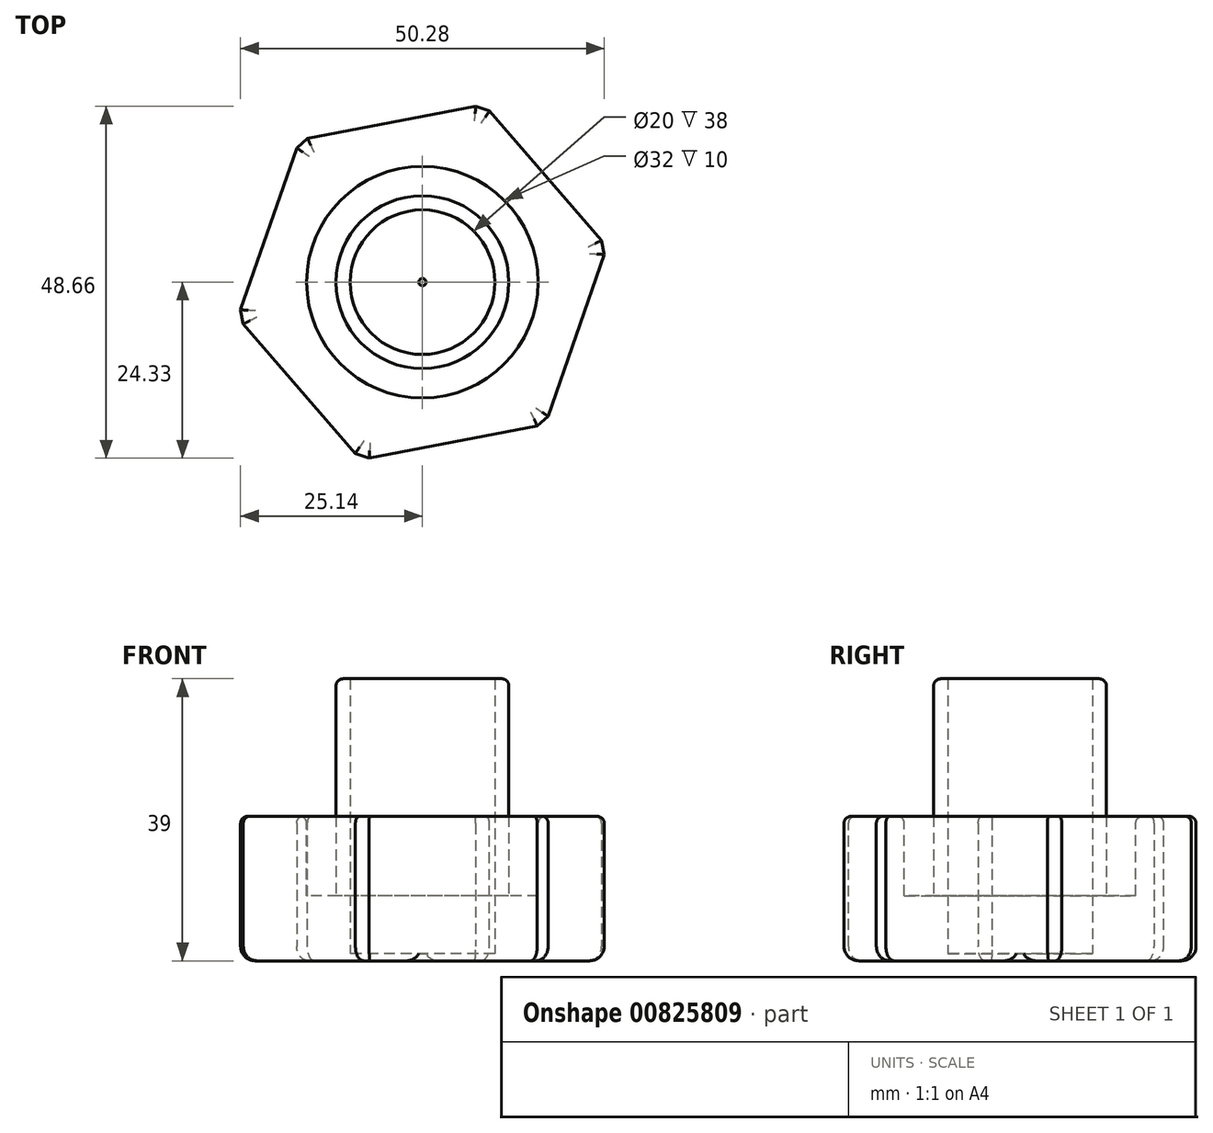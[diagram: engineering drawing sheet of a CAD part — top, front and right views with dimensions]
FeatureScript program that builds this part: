
annotation { "Feature Type Name" : "Feature", "Feature Type Description" : "" }
export const myFeature = defineFeature(function(context is Context, id is Id, definition is map)
    precondition{}
    {
        {
            var Q0;
            Q0=qCreatedBy(makeId("Top.planeOp"),FACE);
            var sketch = newSketch(context, id + "F0", { "sketchPlane" : qUnion([Q0])});
            skCircle(sketch, "E0", {"center": v(0, 0) * mm, "radius": 18.75 * mm});
            skCircle(sketch, "E1", {"center": v(0, 0) * mm, "radius": 10 * mm});
            skSolve(sketch);
        }
        {
            var Q0;
            Q0=makeQuery(id+"F0.imprint","IMPRINT",FACE,{"disambiguationData":[TD([[makeQuery(id+"F0.imprint","IMPRINT",EDGE,{"derivedFrom":sQuery(id+"F0.wireOp",EDGE,"E0")}),1.0]])]});
            extrude(context, id + "F1", {"entities" : qUnion([Q0]), "depth" : 20 * mm, "offsetDistance" : 25 * mm});
        }
        {
            var Q0;
            Q0=makeQuery(id+"F1.opExtrude","CAP_FACE",FACE,{"disambiguationData":[OSD([sQuery(id+"F0.wireOp",EDGE,"E0"),sQuery(id+"F0.wireOp",EDGE,"pwZuV8CJ-bOZG-QT0O-5IBz-90nucOeMPY0X")])],"isStart":false});
            var sketch = newSketch(context, id + "F2", { "sketchPlane" : qUnion([Q0])});
            skCircle(sketch, "E2", {"center": v(0, 0) * mm, "radius": 16 * mm});
            skSolve(sketch);
        }
        {
            var Q0;
            Q0=makeQuery(id+"F2.imprint","IMPRINT",FACE,{"disambiguationData":[TD([[makeQuery(id+"F2.imprint","IMPRINT",EDGE,{"derivedFrom":sQuery(id+"F2.wireOp",EDGE,"E2")}),1.0]])]});
            extrude(context, id + "F3", {"entities" : qUnion([Q0]), "operationType" : NewBodyOperationType.REMOVE, "oppositeDirection" : true, "depth" : 11 * mm, "offsetDistance" : 25 * mm});
        }
        {
            var Q0;
            Q0=makeQuery(id+"F3.boolean.opBoolean","COPY",FACE,{"derivedFrom":makeQuery(id+"F3.opExtrude","CAP_FACE",FACE,{"disambiguationData":[OSD([sQuery(id+"F0.wireOp",EDGE,"E1"),sQuery(id+"F2.wireOp",EDGE,"E2")])],"isStart":false})});
            var sketch = newSketch(context, id + "F4", { "sketchPlane" : qUnion([Q0])});
            skCircle(sketch, "E3", {"center": v(0, 0) * mm, "radius": 11.95 * mm});
            skSolve(sketch);
        }
        {
            var Q0;
            Q0=makeQuery(id+"F4.imprint","IMPRINT",FACE,{"disambiguationData":[TD([[makeQuery(id+"F4.imprint","IMPRINT",EDGE,{"derivedFrom":sQuery(id+"F4.wireOp",EDGE,"E3")}),1.0]])]});
            extrude(context, id + "F5", {"entities" : qUnion([Q0]), "operationType" : NewBodyOperationType.ADD, "depth" : 30 * mm, "offsetDistance" : 25 * mm});
        }
        {
            var Q0;
            Q0=makeQuery(id+"F5.opExtrude","CAP_EDGE",EDGE,{"disambiguationData":[OSD([sQuery(id+"F4.wireOp",EDGE,"E3")])],"isStart":false});
            fillet(context, id + "F6", {"entities" : qUnion([Q0]), "radius" : 1 * mm, "tangentPropagation" : true, "allowEdgeOverflow" : false});
        }
        {
            var Q0;
            Q0=makeQuery(id+"F1.opExtrude","CAP_FACE",FACE,{"disambiguationData":[OSD([sQuery(id+"F0.wireOp",EDGE,"E0"),sQuery(id+"F0.wireOp",EDGE,"pwZuV8CJ-bOZG-QT0O-5IBz-90nucOeMPY0X")])],"isStart":true});
            var sketch = newSketch(context, id + "F7", { "sketchPlane" : qUnion([Q0])});
            skCircle(sketch, "E4", {"center": v(0, 0) * mm, "radius": 0.5 * mm});
            skCircle(sketch, "E5", {"center": v(0, 0) * mm, "radius": 11 * mm});
            skSolve(sketch);
        }
        {
            var Q0;
            Q0=makeQuery(id+"F7.imprint","IMPRINT",FACE,{"disambiguationData":[TD([[makeQuery(id+"F7.imprint","IMPRINT",EDGE,{"derivedFrom":sQuery(id+"F7.wireOp",EDGE,"E4")}),-1.0]])]});
            extrude(context, id + "F8", {"entities" : qUnion([Q0]), "operationType" : NewBodyOperationType.ADD, "oppositeDirection" : true, "depth" : 1 * mm, "offsetDistance" : 25 * mm});
        }
        {
            var Q0;
            {var subQ0=sQuery(id+"F0.wireOp",EDGE,"E1");Q0=makeQuery(id+"F8.boolean.opBoolean","MERGE",FACE,{"derivedFrom":[makeQuery(id+"F1.opExtrude","CAP_FACE",FACE,{"disambiguationData":[OSD([sQuery(id+"F0.wireOp",EDGE,"E0"),subQ0])],"isStart":true}),makeQuery(id+"F8.opExtrude","CAP_FACE",FACE,{"disambiguationData":[OSD([subQ0,sQuery(id+"F7.wireOp",EDGE,"E4")])],"isStart":true})]});}
            var sketch = newSketch(context, id + "F9", { "sketchPlane" : qUnion([Q0])});
            skCircle(sketch, "E6.cCircle", {"center": v(0, 0) * mm, "radius": 22.5 * mm, "construction": true});
            skLineSegment(sketch, "E6.0", {"start": v(8.5, -24.55) * mm, "end": v(-17, -19.64) * mm});
            skLineSegment(sketch, "E6.1", {"start": v(-17, -19.64) * mm, "end": v(-25.51, 4.9) * mm});
            skLineSegment(sketch, "E6.2", {"start": v(-25.51, 4.9) * mm, "end": v(-8.5, 24.55) * mm});
            skLineSegment(sketch, "E6.3", {"start": v(-8.5, 24.55) * mm, "end": v(17, 19.64) * mm});
            skLineSegment(sketch, "E6.4", {"start": v(17, 19.64) * mm, "end": v(25.51, -4.9) * mm});
            skLineSegment(sketch, "E6.5", {"start": v(25.51, -4.9) * mm, "end": v(8.5, -24.55) * mm});
            skPoint(sketch, "E6.0.midPoint", {"position": v(-4.25, -22.1) * mm});
            skSolve(sketch);
        }
        {
            var Q0;
            Q0=makeQuery(id+"F9.imprint","IMPRINT",FACE,{"disambiguationData":[TD([[makeQuery(id+"F9.imprint","IMPRINT",EDGE,{"derivedFrom":sQuery(id+"F9.wireOp",EDGE,"E6.0")}),-1.0]])]});
            extrude(context, id + "F10", {"entities" : qUnion([Q0]), "operationType" : NewBodyOperationType.ADD, "oppositeDirection" : true, "depth" : 20 * mm, "offsetDistance" : 25 * mm});
        }
        {
            var Q0;
            {var subQ0=sQuery(id+"F9.wireOp",EDGE,"E6.5");var subQ1=sQuery(id+"F9.wireOp",EDGE,"E6.0");Q0=makeQuery(id+"F4bdWzwSRBiVOgB_1.boolean.opBoolean","MERGE",EDGE,{"derivedFrom":[makeQuery(id+"F10.opExtrude","SWEPT_EDGE",EDGE,{"disambiguationData":[OSD([subQ1,subQ0])]}),makeQuery(id+"F4bdWzwSRBiVOgB_1.opExtrude","SWEPT_EDGE",EDGE,{"disambiguationData":[OSD([subQ1,subQ0])]})]});}
            var Q1;
            {var subQ0=sQuery(id+"F9.wireOp",EDGE,"E6.1");var subQ1=sQuery(id+"F9.wireOp",EDGE,"E6.0");Q1=makeQuery(id+"F4bdWzwSRBiVOgB_1.boolean.opBoolean","MERGE",EDGE,{"derivedFrom":[makeQuery(id+"F10.opExtrude","SWEPT_EDGE",EDGE,{"disambiguationData":[OSD([subQ1,subQ0])]}),makeQuery(id+"F4bdWzwSRBiVOgB_1.opExtrude","SWEPT_EDGE",EDGE,{"disambiguationData":[OSD([subQ1,subQ0])]})]});}
            var Q2;
            {var subQ0=sQuery(id+"F9.wireOp",EDGE,"E6.2");var subQ1=sQuery(id+"F9.wireOp",EDGE,"E6.1");Q2=makeQuery(id+"F4bdWzwSRBiVOgB_1.boolean.opBoolean","MERGE",EDGE,{"derivedFrom":[makeQuery(id+"F10.opExtrude","SWEPT_EDGE",EDGE,{"disambiguationData":[OSD([subQ1,subQ0])]}),makeQuery(id+"F4bdWzwSRBiVOgB_1.opExtrude","SWEPT_EDGE",EDGE,{"disambiguationData":[OSD([subQ1,subQ0])]})]});}
            var Q3;
            {var subQ0=sQuery(id+"F9.wireOp",EDGE,"E6.3");var subQ1=sQuery(id+"F9.wireOp",EDGE,"E6.2");Q3=makeQuery(id+"F4bdWzwSRBiVOgB_1.boolean.opBoolean","MERGE",EDGE,{"derivedFrom":[makeQuery(id+"F10.opExtrude","SWEPT_EDGE",EDGE,{"disambiguationData":[OSD([subQ1,subQ0])]}),makeQuery(id+"F4bdWzwSRBiVOgB_1.opExtrude","SWEPT_EDGE",EDGE,{"disambiguationData":[OSD([subQ1,subQ0])]})]});}
            var Q4;
            {var subQ0=sQuery(id+"F9.wireOp",EDGE,"E6.4");var subQ1=sQuery(id+"F9.wireOp",EDGE,"E6.3");Q4=makeQuery(id+"F4bdWzwSRBiVOgB_1.boolean.opBoolean","MERGE",EDGE,{"derivedFrom":[makeQuery(id+"F10.opExtrude","SWEPT_EDGE",EDGE,{"disambiguationData":[OSD([subQ1,subQ0])]}),makeQuery(id+"F4bdWzwSRBiVOgB_1.opExtrude","SWEPT_EDGE",EDGE,{"disambiguationData":[OSD([subQ1,subQ0])]})]});}
            var Q5;
            {var subQ0=sQuery(id+"F9.wireOp",EDGE,"E6.5");var subQ1=sQuery(id+"F9.wireOp",EDGE,"E6.4");Q5=makeQuery(id+"F4bdWzwSRBiVOgB_1.boolean.opBoolean","MERGE",EDGE,{"derivedFrom":[makeQuery(id+"F10.opExtrude","SWEPT_EDGE",EDGE,{"disambiguationData":[OSD([subQ1,subQ0])]}),makeQuery(id+"F4bdWzwSRBiVOgB_1.opExtrude","SWEPT_EDGE",EDGE,{"disambiguationData":[OSD([subQ1,subQ0])]})]});}
            chamfer(context, id + "F11", {"entities" : qUnion([Q0, Q1, Q2, Q3, Q4, Q5]), "width" : 2 * mm, "tangentPropagation" : true});
        }
        {
            var Q0;
            {var subQ0=sQuery(id+"F0.wireOp",EDGE,"E0");var subQ1=sQuery(id+"F0.wireOp",EDGE,"E1");Q0=makeQuery(id+"F10.boolean.opBoolean","MERGE",FACE,{"derivedFrom":[makeQuery(id+"F8.boolean.opBoolean","MERGE",FACE,{"derivedFrom":[makeQuery(id+"F1.opExtrude","CAP_FACE",FACE,{"disambiguationData":[OSD([subQ0,subQ1])],"isStart":true}),makeQuery(id+"F8.opExtrude","CAP_FACE",FACE,{"disambiguationData":[OSD([subQ1,sQuery(id+"F7.wireOp",EDGE,"E4")])],"isStart":true})]}),makeQuery(id+"F10.opExtrude","CAP_FACE",FACE,{"disambiguationData":[OSD([subQ0,sQuery(id+"F9.wireOp",EDGE,"E6.0"),sQuery(id+"F9.wireOp",EDGE,"E6.1"),sQuery(id+"F9.wireOp",EDGE,"E6.2"),sQuery(id+"F9.wireOp",EDGE,"E6.3"),sQuery(id+"F9.wireOp",EDGE,"E6.4"),sQuery(id+"F9.wireOp",EDGE,"E6.5")])],"isStart":true})]});}
            fillet(context, id + "F12", {"entities" : qUnion([Q0]), "radius" : 2 * mm, "tangentPropagation" : true, "allowEdgeOverflow" : false});
        }
        {
            var Q0;
            Q0=makeQuery(id+"F10.opExtrude","CAP_FACE",FACE,{"disambiguationData":[OSD([sQuery(id+"F0.wireOp",EDGE,"E0"),sQuery(id+"F9.wireOp",EDGE,"E6.0"),sQuery(id+"F9.wireOp",EDGE,"E6.1"),sQuery(id+"F9.wireOp",EDGE,"E6.2"),sQuery(id+"F9.wireOp",EDGE,"E6.3"),sQuery(id+"F9.wireOp",EDGE,"E6.4"),sQuery(id+"F9.wireOp",EDGE,"E6.5")])],"isStart":false});
            fillet(context, id + "F13", {"entities" : qUnion([Q0]), "radius" : 1 * mm, "tangentPropagation" : true, "allowEdgeOverflow" : false});
        }
    });
